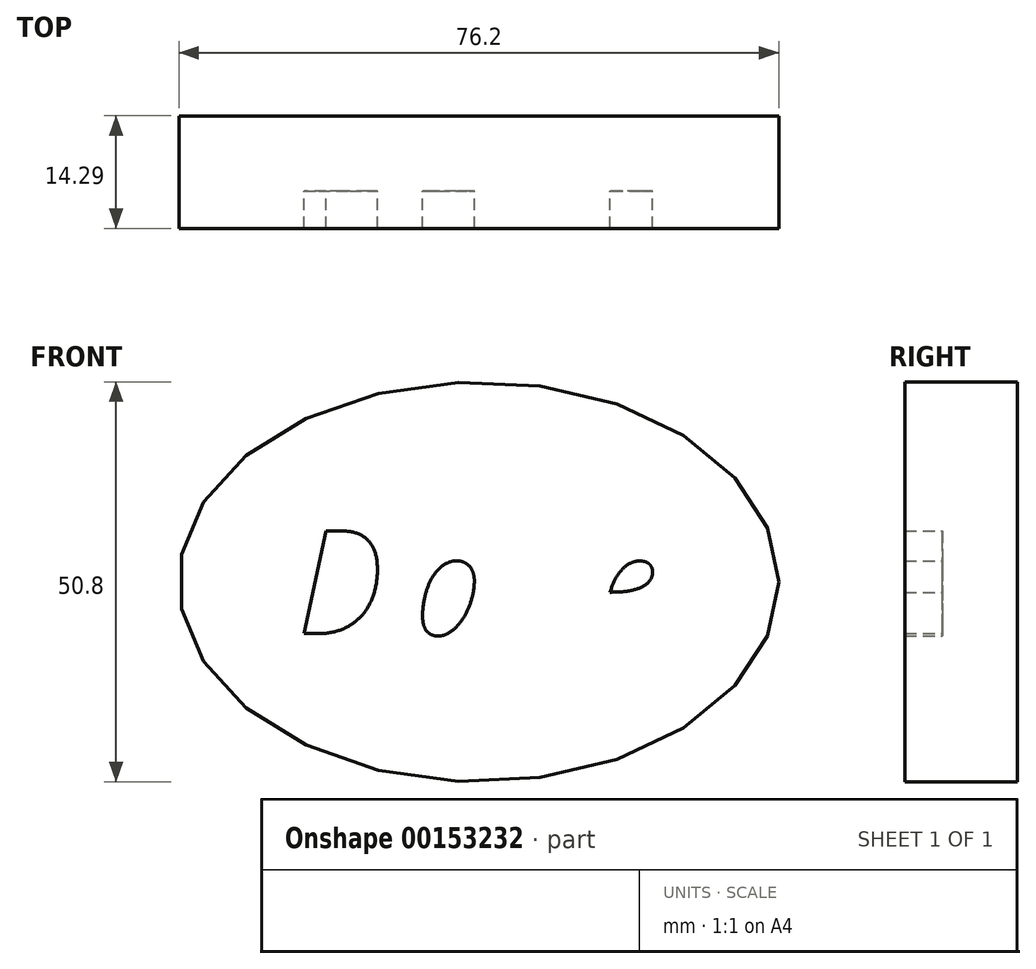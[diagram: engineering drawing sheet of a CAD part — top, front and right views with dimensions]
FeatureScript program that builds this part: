
annotation { "Feature Type Name" : "Feature", "Feature Type Description" : "" }
export const myFeature = defineFeature(function(context is Context, id is Id, definition is map)
    precondition{}
    {
        {
            var Q0;
            Q0=qCreatedBy(makeId("Front.planeOp"),FACE);
            var sketch = newSketch(context, id + "F0", { "sketchPlane" : qUnion([Q0])});
            skEllipse(sketch, "E0", {"center": v(0, 0) * mm, "majorRadius": 38.1 * mm, "minorRadius": 25.4 * mm, "majorAxis": v(1, 0)});
            skSolve(sketch);
        }
        {
            var Q0;
            Q0=makeQuery(id+"F0.imprint","IMPRINT",FACE,{"disambiguationData":[TD([[makeQuery(id+"F0.imprint","IMPRINT",EDGE,{"derivedFrom":sQuery(id+"F0.wireOp",EDGE,"E0")}),1.0]])]});
            var Q1;
            Q1=sQuery(id+"F0.wireOp",EDGE,"E0");
            extrude(context, id + "F1", {"entities" : qUnion([Q0]), "surfaceEntities" : qUnion([Q1]), "oppositeDirection" : true, "depth" : 9.52 * mm});
        }
        {
            var Q0;
            Q0=makeQuery(id+"F1.opExtrude","CAP_FACE",FACE,{"disambiguationData":[OSD([sQuery(id+"F0.wireOp",EDGE,"E0")])],"isStart":true});
            var sketch = newSketch(context, id + "F2", { "sketchPlane" : qUnion([Q0])});
            skText(sketch, "E1", { "text": "Dave", "fontName": "OpenSans-Italic.ttf"});
            const initialGuessF2  = {"E1": [-0.0254, -0.00823, 1, 0, 0.01647]};
            skSetInitialGuess(sketch, initialGuessF2);
            skSolve(sketch);
        }
        {
            var Q0;
            Q0 = qSketchRegion(id + "F2", true);
            var Q1;
            Q1=makeQuery(id+"F2.imprint","IMPRINT",FACE,{"disambiguationData":[TD([[makeQuery(id+"F2.imprint","IMPRINT",EDGE,{"derivedFrom":sQuery(id+"F2.wireOp",EDGE,"E1.sketch_text.stroke-0")}),1.0]])]});
            extrude(context, id + "F3", {"entities" : qUnion([Q0, Q1]), "operationType" : NewBodyOperationType.ADD, "depth" : 4.76 * mm});
        }
    });
